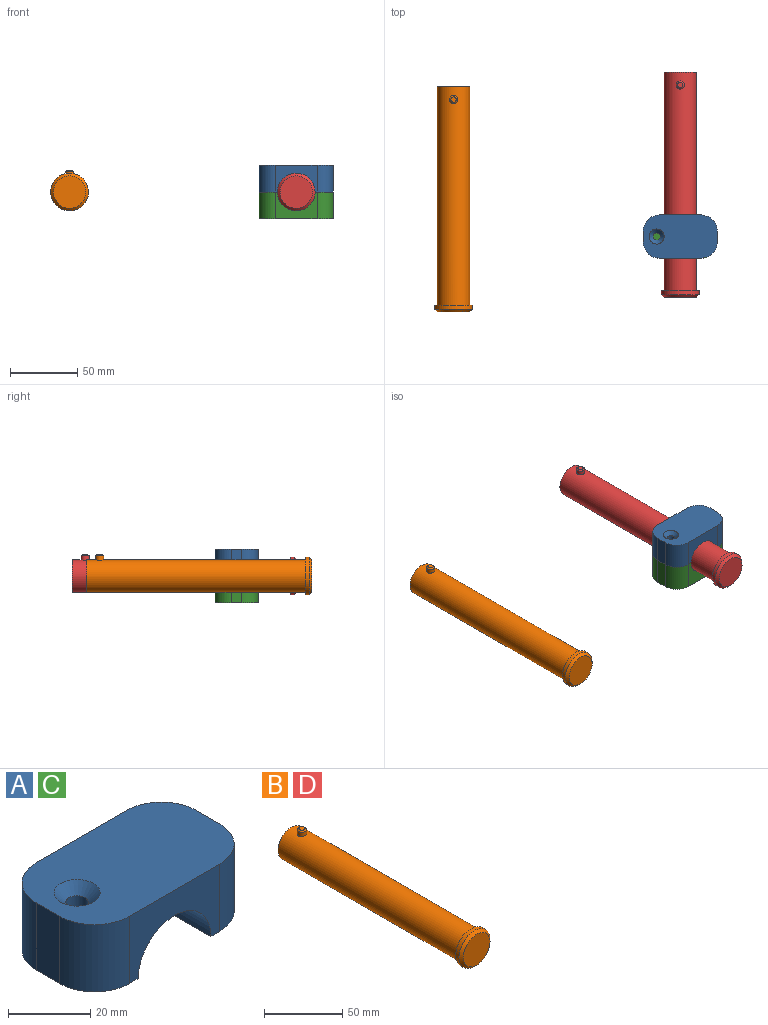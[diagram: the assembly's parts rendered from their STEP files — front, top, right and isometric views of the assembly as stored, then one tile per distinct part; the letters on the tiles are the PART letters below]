
ASSEMBLY  parts=4 mates=3
PART A: 14 faces, bbox 55x32x20 mm
  f0: plane 32x15mm, normal (0,0,-1), area 418.2mm2, adj f2,f3,f6,f7,f10,f12
  f1: plane 32x15mm, normal (0,0,-1), area 394.4mm2, adj f2,f5,f6,f7,f8,f11,f13
  f2: plane 31x20mm, normal (0,1,0), area 374.6mm2, adj f0,f1,f4,f7,f10,f11
  f3: plane 20x8mm, normal (1,0,0), area 160mm2, adj f0,f4,f10,f12
  f4: plane 55x32mm, normal (0,0,1), area 1537.9mm2, adj f2,f3,f5,f6,f9,f10,f11,f12
  f5: plane 20x8mm, normal (-1,0,0), area 160mm2, adj f1,f4,f11,f13
  f6: plane 31x20mm, normal (0,-1,0), area 374.6mm2, adj f0,f1,f4,f7,f12,f13
  f7: cylinder r=12.5mm len=32mm, axis (0,-1,0), area 1256.6mm2, adj f0,f1,f2,f6
  f8: cylinder r=2.75mm len=17.15mm, axis (0,0,1), area 296.3mm2, adj f1,f9
  f9: cone r=2.75mm half-angle=45deg, axis (0,0,1), area 105.7mm2, adj f4,f8
  f10: cylinder r=12mm len=20mm, axis (0,0,1), area 377mm2, adj f0,f2,f3,f4
  f11: cylinder r=12mm len=20mm, axis (0,0,-1), area 377mm2, adj f1,f2,f4,f5
  f12: cylinder r=12mm len=20mm, axis (0,0,-1), area 377mm2, adj f0,f3,f4,f6
  f13: cylinder r=12mm len=20mm, axis (0,0,1), area 377mm2, adj f1,f4,f5,f6
PART B: 12 faces, bbox 28x167.1x30 mm
  f0: cylinder r=12mm len=162.1mm, axis (0,1,0), area 12193.5mm2, adj f1,f3,f5
  f1: plane 24x24mm, normal (0,1,0), area 452.4mm2, adj f0
  f2: cylinder r=14mm len=28mm, axis (0,-1,0), area 263.9mm2, adj f3,f8
  f3: plane 28x28mm, normal (0,1,0), area 163.4mm2, adj f0,f2
  f4: plane 24x24mm, normal (0,-1,0), area 452.4mm2, adj f8
  f5: cylinder r=3mm len=6mm, axis (0,0,-1), area 60.1mm2, adj f0,f7
  f6: plane 4x4mm, normal (0,0,1), area 12.6mm2, adj f7
  f7: cone r=2mm half-angle=45deg, axis (0,0,-1), area 22.2mm2, adj f5,f6
  f8: cone r=12mm half-angle=45deg, axis (0,1,0), area 231mm2, adj f2,f4
  f9: cylinder r=3mm len=16.4mm, axis (0,0,1), area 309.1mm2, adj f10,f11
  f10: plane 6x6mm, normal (0,0,1), area 28.3mm2, adj f9
  f11: plane 6x6mm, normal (0,0,-1), area 28.3mm2, adj f9
PART C: same geometry as A
PART D: same geometry as B
PLACE A at identity fixed
PLACE B t=(-168.2,56.6,0)mm
PLACE C rot(axis=(0,1,0),180deg) t=(0,0,-20)mm
PLACE D rot(axis=(0,1,0),0deg) t=(0,67.45,0)mm
MATE planar C.f2 <-> A.f2  axis (0,1,0) through (0,16,-23.08)mm
MATE slider D.f0 <-> C.f7  axis (0,1,0) through (0,41,-10)mm
MATE cylindrical C.f7 <-> A.f7  axis (0,-1,0) through (0,16,-10)mm
